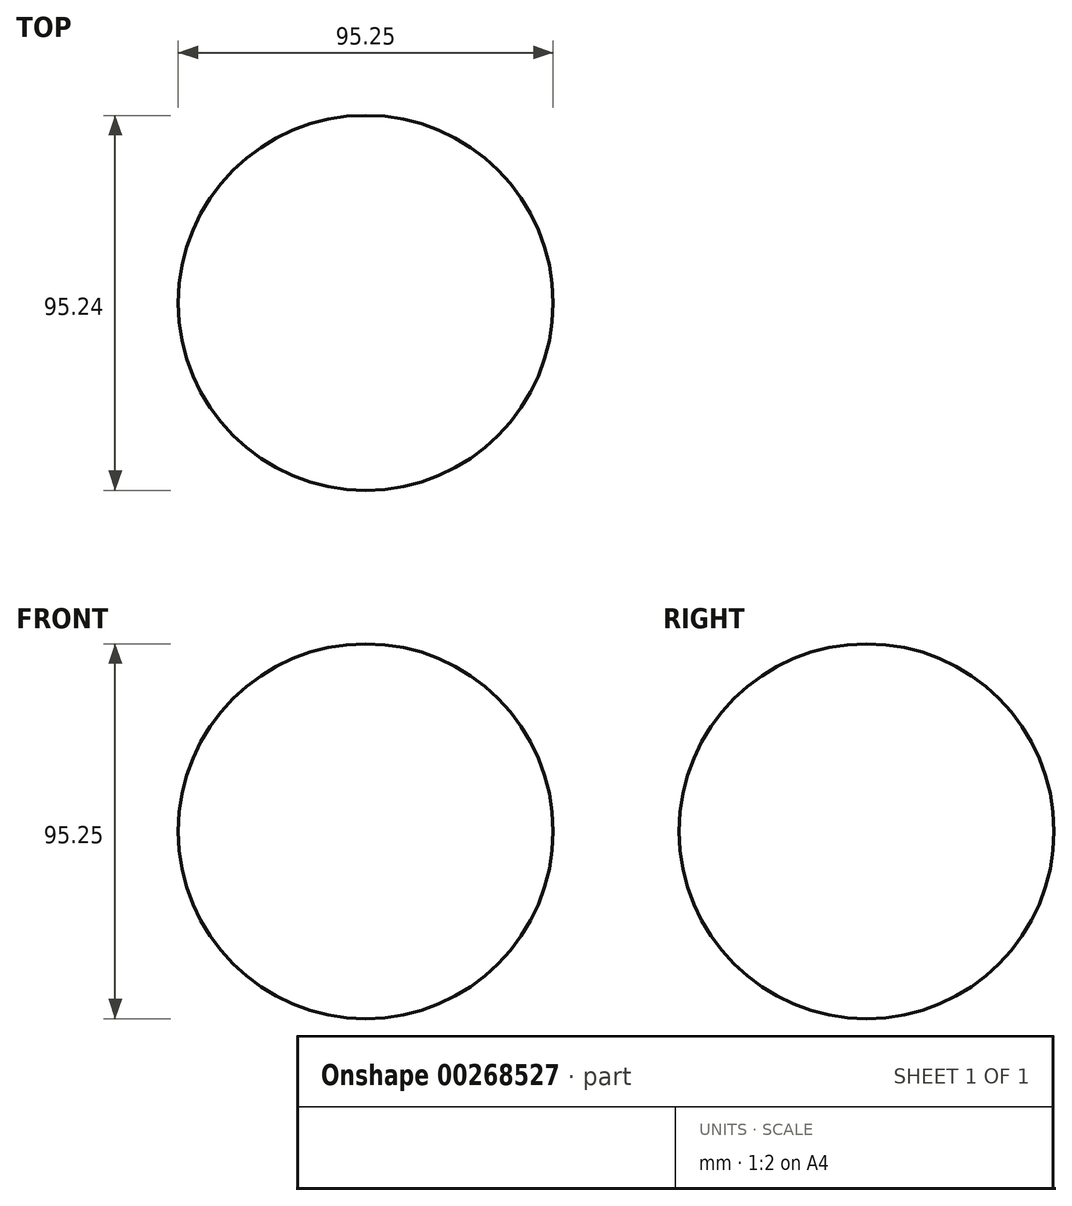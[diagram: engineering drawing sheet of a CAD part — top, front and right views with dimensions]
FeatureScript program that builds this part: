
annotation { "Feature Type Name" : "Feature", "Feature Type Description" : "" }
export const myFeature = defineFeature(function(context is Context, id is Id, definition is map)
    precondition{}
    {
        {
            var Q0;
            Q0=qCreatedBy(makeId("Front.planeOp"),FACE);
            var sketch = newSketch(context, id + "F0", { "sketchPlane" : qUnion([Q0])});
            skLineSegment(sketch, "E0", {"start": v(0, 0) * mm, "end": v(0, 47.63) * mm});
            skArc(sketch, "E1", {"start": v(0, 47.63) * mm, "mid": v(33.68, 33.68) * mm, "end": v(47.63, 0) * mm});
            skLineSegment(sketch, "E2", {"start": v(0, 0) * mm, "end": v(47.63, 0) * mm});
            skSolve(sketch);
        }
        {
            var Q0;
            Q0=makeQuery(id+"F0.imprint","IMPRINT",FACE,{"disambiguationData":[TD([[makeQuery(id+"F0.imprint","IMPRINT",EDGE,{"derivedFrom":sQuery(id+"F0.wireOp",EDGE,"E0")}),-1.0]])]});
            var Q1;
            Q1=sQuery(id+"F0.wireOp",EDGE,"E2");
            revolve(context, id + "F1", {"entities" : qUnion([Q0]), "axis" : qUnion([Q1]), "revolveType" : RevolveType.FULL});
        }
        {
            var Q0;
            Q0=makeQuery(id+"F1.opRevolve","SWEPT_BODY",BODY,{"disambiguationData":[OSD([sQuery(id+"F0.wireOp",EDGE,"E0"),sQuery(id+"F0.wireOp",EDGE,"E1"),sQuery(id+"F0.wireOp",EDGE,"E2")])]});
            var Q1;
            Q1=makeQuery(id+"F1.opRevolve","SWEPT_FACE",FACE,{"disambiguationData":[OSD([sQuery(id+"F0.wireOp",EDGE,"E0")])]});
            mirror(context, id + "F2", {"operationType" : NewBodyOperationType.ADD, "entities" : qUnion([Q0]), "mirrorPlane" : qUnion([Q1])});
        }
    });
